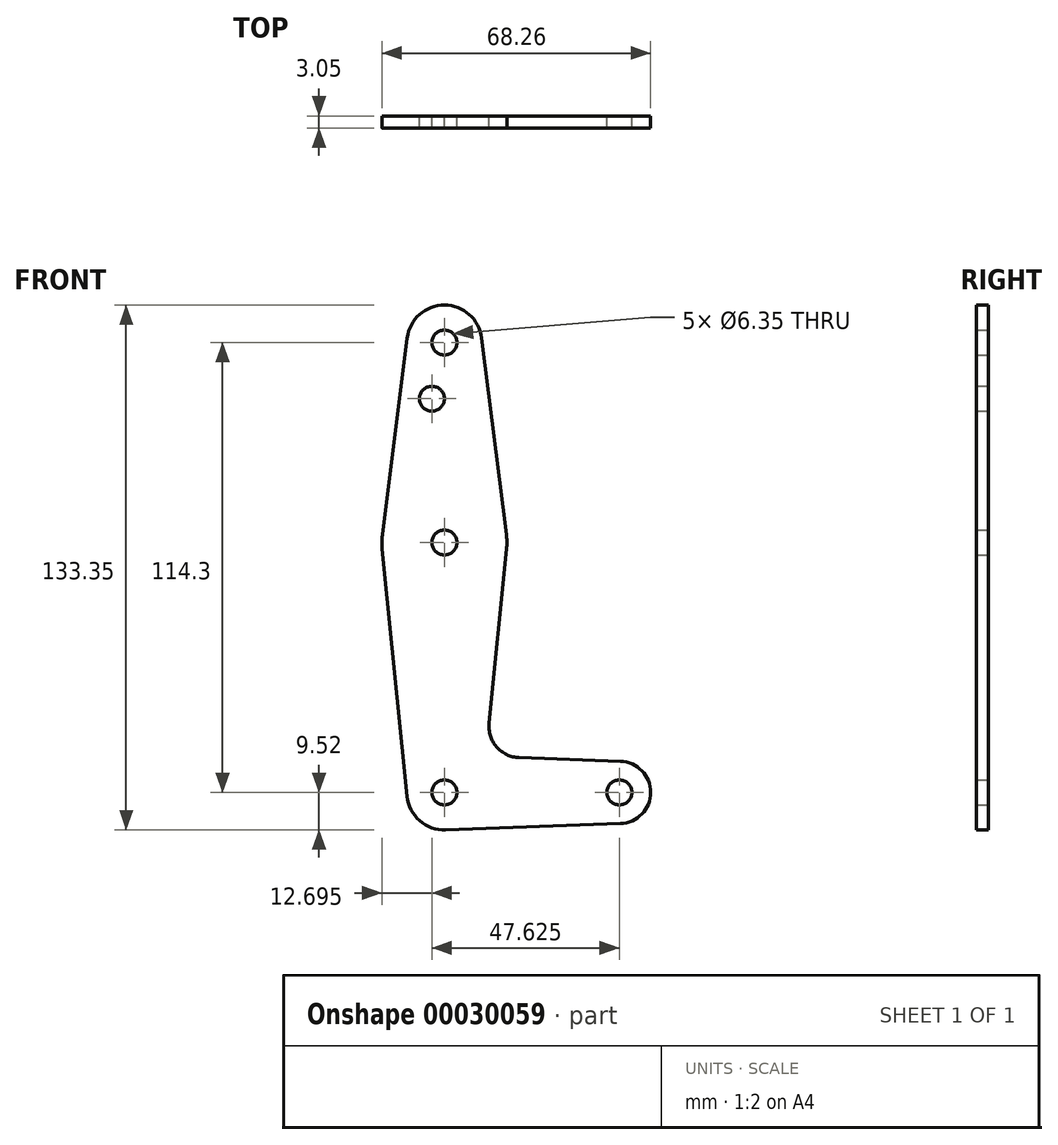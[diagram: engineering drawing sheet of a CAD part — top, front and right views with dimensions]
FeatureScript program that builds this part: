
annotation { "Feature Type Name" : "Feature", "Feature Type Description" : "" }
export const myFeature = defineFeature(function(context is Context, id is Id, definition is map)
    precondition{}
    {
        {
            var Q0;
            Q0=qCreatedBy(makeId("Front.planeOp"),FACE);
            var sketch = newSketch(context, id + "F0", { "sketchPlane" : qUnion([Q0])});
            skLineSegment(sketch, "E0", {"start": v(0, 0) * mm, "end": v(0, 63.5) * mm, "construction": true});
            skLineSegment(sketch, "E1", {"start": v(0, 63.5) * mm, "end": v(0, 114.3) * mm, "construction": true});
            skLineSegment(sketch, "E2", {"start": v(0, 0) * mm, "end": v(44.45, 0) * mm, "construction": true});
            skCircle(sketch, "E3", {"center": v(44.45, 0) * mm, "radius": 7.94 * mm});
            skCircle(sketch, "E4", {"center": v(0, 0) * mm, "radius": 9.53 * mm});
            skCircle(sketch, "E5", {"center": v(0, 63.5) * mm, "radius": 15.88 * mm});
            skCircle(sketch, "E6", {"center": v(0, 114.3) * mm, "radius": 9.53 * mm});
            skLineSegment(sketch, "E7", {"start": v(9.45, 115.5) * mm, "end": v(15.75, 65.48) * mm});
            skLineSegment(sketch, "E8", {"start": v(15.8, 61.91) * mm, "end": v(11.34, 17.6) * mm});
            skLineSegment(sketch, "E9", {"start": v(18.97, 8.85) * mm, "end": v(44.73, 7.93) * mm});
            skLineSegment(sketch, "E10.MirrorCS", {"start": v(-9.45, 115.5) * mm, "end": v(-15.75, 65.48) * mm});
            skLineSegment(sketch, "E11.MirrorCS", {"start": v(-15.8, 61.91) * mm, "end": v(-9.48, -0.95) * mm});
            skLineSegment(sketch, "E12.MirrorCS", {"start": v(0.34, -9.52) * mm, "end": v(44.73, -7.93) * mm});
            skCircle(sketch, "E13", {"center": v(44.45, 0) * mm, "radius": 3.18 * mm});
            skCircle(sketch, "E14", {"center": v(0, 0) * mm, "radius": 3.18 * mm});
            skCircle(sketch, "E15", {"center": v(0, 63.5) * mm, "radius": 3.18 * mm});
            skCircle(sketch, "E16", {"center": v(0, 114.3) * mm, "radius": 3.18 * mm});
            skCircle(sketch, "E17", {"center": v(-3.18, 100.03) * mm, "radius": 3.18 * mm});
            skPoint(sketch, "E18.newPointA", {"position": v(9.48, -0.95) * mm});
            skPoint(sketch, "E18.newPointB", {"position": v(0.34, 9.52) * mm});
            skArc(sketch, "E18.filletArc", {"start": v(11.34, 17.6) * mm, "mid": v(13.26, 11.57) * mm, "end": v(18.97, 8.85) * mm});
            skSolve(sketch);
        }
        {
            var Q0;
            Q0=makeQuery(id+"F0.imprint","IMPRINT",FACE,{"disambiguationData":[TD([[makeQuery(id+"F0.imprint","IMPRINT",EDGE,{"derivedFrom":sQuery(id+"F0.wireOp",EDGE,"E16")}),-1.0]])]});
            var Q1;
            {var subQ1=sQuery(id+"F0.wireOp",EDGE,"E7");Q1=makeQuery(id+"F0.imprint","IMPRINT",FACE,{"disambiguationData":[TD([[makeQuery(id+"F0.imprint","IMPRINT",EDGE,{"derivedFrom":subQ1}),-1.0]])]});}
            var Q2;
            Q2=makeQuery(id+"F0.imprint","IMPRINT",FACE,{"disambiguationData":[TD([[makeQuery(id+"F0.imprint","IMPRINT",EDGE,{"derivedFrom":sQuery(id+"F0.wireOp",EDGE,"E15")}),-1.0]])]});
            var Q3;
            {var subQ2=sQuery(id+"F0.wireOp",EDGE,"E8");Q3=makeQuery(id+"F0.imprint","IMPRINT",FACE,{"disambiguationData":[TD([[makeQuery(id+"F0.imprint","IMPRINT",EDGE,{"derivedFrom":subQ2}),-1.0]])]});}
            var Q4;
            Q4=makeQuery(id+"F0.imprint","IMPRINT",FACE,{"disambiguationData":[TD([[makeQuery(id+"F0.imprint","IMPRINT",EDGE,{"derivedFrom":sQuery(id+"F0.wireOp",EDGE,"E14")}),-1.0]])]});
            var Q5;
            Q5=makeQuery(id+"F0.imprint","IMPRINT",FACE,{"disambiguationData":[TD([[makeQuery(id+"F0.imprint","IMPRINT",EDGE,{"derivedFrom":sQuery(id+"F0.wireOp",EDGE,"E13")}),-1.0]])]});
            extrude(context, id + "F1", {"entities" : qUnion([Q0, Q1, Q2, Q3, Q4, Q5]), "depth" : 3.05 * mm});
        }
    });
